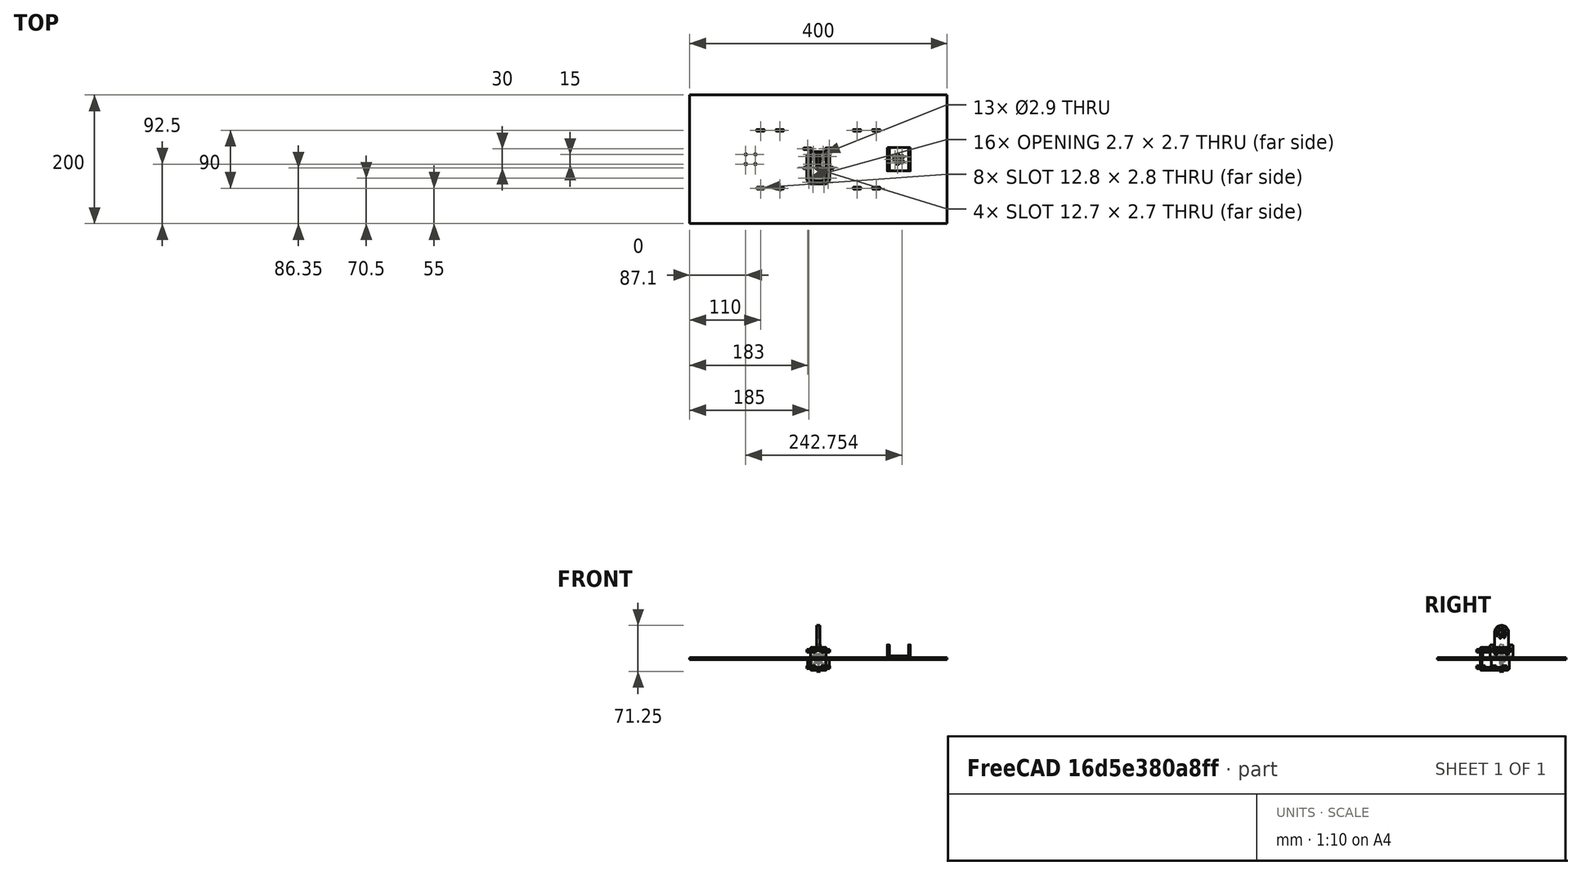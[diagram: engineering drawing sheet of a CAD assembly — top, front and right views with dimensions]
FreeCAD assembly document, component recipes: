
FREECAD ASSEMBLY — COMPONENT RECIPES ("Unnamed")

This assembly document has 8 components, labeled P0..P7 below (a component is one placed body or linked part). 6 of them carry a construction recipe — the FreeCAD feature program that regenerates the part from scratch, quoted from this document or its linked companion documents; the rest are supplied as boundary geometry only. No exploded tour is included for this assembly.
COMPONENT P0 — recipe-attached ("Body", modeled in this document).
Construction recipe (the document's own serialized feature program — sketch geometry with constraints, then the solid features built on it; lengths are millimeters unless a unit is written):

FEATURE [Sketcher::SketchObject] Sketch
  ArcFitTolerance = 1e-06
  AttachmentSupport = -> [Origin]
  ExternalTypes = [0]
  FullyConstrained = true
  MakeInternals = false
  MapMode = 5
  _ExternalGeoVersion = 1
  sketch-geometry (5):
    g0: LineSegment StartX=-200 StartY=-100 StartZ=0 EndX=200 EndY=-100 EndZ=0
    g1: LineSegment StartX=200 StartY=-100 StartZ=0 EndX=200 EndY=100 EndZ=0
    g2: LineSegment StartX=200 StartY=100 StartZ=0 EndX=-200 EndY=100 EndZ=0
    g3: LineSegment StartX=-200 StartY=100 StartZ=0 EndX=-200 EndY=-100 EndZ=0
    g4: GeomPoint [constr] X=0 Y=0 Z=0
  constraints (12):
    c: Coincident(g0,g1)
    c: Coincident(g1,g2)
    c: Coincident(g2,g3)
    c: Coincident(g3,g0)
    c: Horizontal(g0)
    c: Horizontal(g2)
    c: Vertical(g1)
    c: Vertical(g3)
    c: Symmetric(g2,g0,g4)
    c: Distance(g1,g3) = 400
    c: Distance(g0,g2) = 200
    c: Coincident(g4,g-1)
FEATURE [PartDesign::Pad] Pad
  Direction = (0,0,1)
  Length = 3
  Length2 = 10
  Profile = -> Sketch
  ReferenceAxis = -> Sketch [N_Axis]
  Refine = true
  SideType = 0
  Suppressed = false
  Type = 0
  Type2 = 0
FEATURE [Sketcher::SketchObject] Sketch001
  ArcFitTolerance = 1e-06
  AttachmentSupport = -> [Pad]
  ExternalTypes = [0]
  FullyConstrained = true
  MakeInternals = false
  MapMode = 5
  Placement = pos=(0,0,3) rot=(0,0,1;0rad)
  _ExternalGeoVersion = 1
  sketch-geometry (16):
    g0: ArcOfCircle CenterX=-12 CenterY=16.35 CenterZ=0 NormalX=0 NormalY=0 NormalZ=1 AngleXU=0 Radius=1.35 StartAngle=4.71239 EndAngle=7.85398
    g1: ArcOfCircle CenterX=-22 CenterY=16.35 CenterZ=0 NormalX=0 NormalY=0 NormalZ=1 AngleXU=0 Radius=1.35 StartAngle=1.5708 EndAngle=4.71239
    g2: LineSegment StartX=-12 StartY=15 StartZ=0 EndX=-22 EndY=15 EndZ=0
    g3: LineSegment StartX=-12 StartY=17.7 StartZ=0 EndX=-22 EndY=17.7 EndZ=0
    g4: ArcOfCircle CenterX=12 CenterY=16.35 CenterZ=0 NormalX=0 NormalY=0 NormalZ=1 AngleXU=0 Radius=1.35 StartAngle=1.5708 EndAngle=4.71239
    g5: ArcOfCircle CenterX=22 CenterY=16.35 CenterZ=0 NormalX=0 NormalY=0 NormalZ=1 AngleXU=0 Radius=1.35 StartAngle=4.71239 EndAngle=7.85398
    g6: LineSegment StartX=12 StartY=17.7 StartZ=0 EndX=22 EndY=17.7 EndZ=0
    g7: LineSegment StartX=12 StartY=15 StartZ=0 EndX=22 EndY=15 EndZ=0
    g8: ArcOfCircle CenterX=-22 CenterY=-13.65 CenterZ=0 NormalX=0 NormalY=0 NormalZ=1 AngleXU=0 Radius=1.35 StartAngle=1.5708 EndAngle=4.71239
    g9: ArcOfCircle CenterX=-12 CenterY=-13.65 CenterZ=0 NormalX=0 NormalY=0 NormalZ=1 AngleXU=0 Radius=1.35 StartAngle=4.71239 EndAngle=7.85398
    g10: LineSegment StartX=-22 StartY=-12.3 StartZ=0 EndX=-12 EndY=-12.3 EndZ=0
    g11: LineSegment StartX=-22 StartY=-15 StartZ=0 EndX=-12 EndY=-15 EndZ=0
    g12: ArcOfCircle CenterX=12 CenterY=-13.65 CenterZ=0 NormalX=0 NormalY=0 NormalZ=1 AngleXU=0 Radius=1.35 StartAngle=1.5708 EndAngle=4.71239
    g13: ArcOfCircle CenterX=22 CenterY=-13.65 CenterZ=0 NormalX=0 NormalY=0 NormalZ=1 AngleXU=0 Radius=1.35 StartAngle=4.71239 EndAngle=7.85398
    g14: LineSegment StartX=12 StartY=-12.3 StartZ=0 EndX=22 EndY=-12.3 EndZ=0
    g15: LineSegment StartX=12 StartY=-15 StartZ=0 EndX=22 EndY=-15 EndZ=0
  constraints (40):
    c: Tangent(g0,g2) = 1.5708
    c: Tangent(g0,g3) = -1.5708
    c: Tangent(g1,g2) = 1.5708
    c: Tangent(g1,g3) = -1.5708
    c: Equal(g0,g1)
    c: Distance(g0,g1) = 10
    c: Radius(g0) = 1.35
    c: Horizontal(g2)
    c: Distance(g0,g-2) = 12
    c: Tangent(g4,g6) = 1.5708
    c: Tangent(g4,g7) = -1.5708
    c: Tangent(g5,g6) = 1.5708
    c: Tangent(g5,g7) = -1.5708
    c: Equal(g4,g5)
    c: Distance(g4,g5) = 10
    c: Radius(g4) = 1.35
    c: Horizontal(g6)
    c: Distance(g4,g-2) = 12
    c: Distance(g-1,g7) = 15
    c: Distance(g-1,g2) = 15
    c: Tangent(g8,g10) = 1.5708
    c: Tangent(g8,g11) = -1.5708
    c: Tangent(g9,g10) = 1.5708
    c: Tangent(g9,g11) = -1.5708
    c: Equal(g8,g9)
    c: Distance(g8,g9) = 10
    c: Radius(g8) = 1.35
    c: Horizontal(g10)
    c: Distance(g9,g-2) = 12
    c: DistanceY(g9,g0) = 30
    c: Tangent(g12,g14) = 1.5708
    c: Tangent(g12,g15) = -1.5708
    c: Tangent(g13,g14) = 1.5708
    c: Tangent(g13,g15) = -1.5708
    c: Equal(g12,g13)
    c: Distance(g12,g13) = 10
    c: Radius(g12) = 1.35
    c: Horizontal(g14)
    c: Distance(g12,g-2) = 12
    c: Distance(g12,g4) = 30
FEATURE [PartDesign::Pocket] Pocket
  BaseFeature = -> Pad
  Direction = (0,0,-1)
  Length = 5
  Length2 = 5
  Profile = -> Sketch001
  ReferenceAxis = -> Sketch001 [N_Axis]
  Refine = true
  SideType = 0
  Suppressed = false
  Type = 0
  Type2 = 0
FEATURE [Sketcher::SketchObject] Sketch002
  ArcFitTolerance = 1e-06
  AttachmentSupport = -> [Pocket]
  ExternalTypes = [0]
  FullyConstrained = true
  MakeInternals = false
  MapMode = 5
  Placement = pos=(0,0,3) rot=(0,0,1;0rad)
  _ExternalGeoVersion = 1
  sketch-geometry (8):
    g0: ArcOfCircle CenterX=-55 CenterY=-45 CenterZ=0 NormalX=0 NormalY=0 NormalZ=1 AngleXU=0 Radius=1.4 StartAngle=4.71239 EndAngle=7.85398
    g1: ArcOfCircle CenterX=-65 CenterY=-45 CenterZ=0 NormalX=0 NormalY=0 NormalZ=1 AngleXU=0 Radius=1.4 StartAngle=1.5708 EndAngle=4.71239
    g2: LineSegment StartX=-55 StartY=-46.4 StartZ=0 EndX=-65 EndY=-46.4 EndZ=0
    g3: LineSegment StartX=-55 StartY=-43.6 StartZ=0 EndX=-65 EndY=-43.6 EndZ=0
    g4: ArcOfCircle CenterX=-85 CenterY=-45 CenterZ=0 NormalX=0 NormalY=0 NormalZ=1 AngleXU=0 Radius=1.4 StartAngle=4.71239 EndAngle=7.85398
    g5: ArcOfCircle CenterX=-95 CenterY=-45 CenterZ=0 NormalX=0 NormalY=0 NormalZ=1 AngleXU=0 Radius=1.4 StartAngle=1.5708 EndAngle=4.71239
    g6: LineSegment StartX=-85 StartY=-46.4 StartZ=0 EndX=-95 EndY=-46.4 EndZ=0
    g7: LineSegment StartX=-85 StartY=-43.6 StartZ=0 EndX=-95 EndY=-43.6 EndZ=0
  constraints (20):
    c: Tangent(g0,g2) = 1.5708
    c: Tangent(g0,g3) = -1.5708
    c: Tangent(g1,g2) = 1.5708
    c: Tangent(g1,g3) = -1.5708
    c: Equal(g0,g1)
    c: Distance(g0,g1) = 10
    c: Radius(g0) = 1.4
    c: Horizontal(g2)
    c: Distance(g0,g-2) = 55
    c: Distance(g0,g-1) = 45
    c: Tangent(g4,g6) = 1.5708
    c: Tangent(g4,g7) = -1.5708
    c: Tangent(g5,g6) = 1.5708
    c: Tangent(g5,g7) = -1.5708
    c: Equal(g4,g5)
    c: Distance(g4,g5) = 10
    c: Radius(g4) = 1.4
    c: Horizontal(g6)
    c: DistanceX(g4,g1) = 20
    c: Distance(g5,g-1) = 45
FEATURE [PartDesign::Pocket] Pocket001
  BaseFeature = -> Pocket
  Direction = (0,0,-1)
  Length = 5
  Length2 = 5
  Profile = -> Sketch002
  ReferenceAxis = -> Sketch002 [N_Axis]
  Refine = true
  SideType = 0
  Suppressed = false
  Type = 0
  Type2 = 0
FEATURE [PartDesign::Mirrored] Mirrored
  BaseFeature = -> Pocket001
  MirrorPlane = -> Sketch002 [V_Axis]
  Originals = -> [Pocket001]
  Refine = true
  Suppressed = false
  TransformMode = 0
FEATURE [PartDesign::Mirrored] Mirrored001
  BaseFeature = -> Mirrored
  MirrorPlane = -> Sketch002 [H_Axis]
  Originals = -> [Pocket001]
  Refine = true
  Suppressed = false
  TransformMode = 0
FEATURE [PartDesign::PolarPattern] PolarPattern
  Angle = 360
  Axis = -> Sketch002 [N_Axis]
  BaseFeature = -> Mirrored001
  Mode = 0
  Occurrences = 2
  Offset = 120
  Originals = -> [Pocket001]
  Refine = true
  SpacingPattern = [0]
  Spacings = [-1]
  Suppressed = false
  TransformMode = 0
FEATURE [Sketcher::SketchObject] Sketch006
  ArcFitTolerance = 1e-06
  AttachmentSupport = -> [PolarPattern]
  ExternalTypes = [0]
  FullyConstrained = true
  MakeInternals = false
  MapMode = 5
  Placement = pos=(0,0,3) rot=(0,0,1;0rad)
  _ExternalGeoVersion = 1
  sketch-geometry (5):
    g0: Circle CenterX=123.15 CenterY=5.7 CenterZ=0 NormalX=0 NormalY=0 NormalZ=1 AngleXU=0 Radius=1.25
    g1: Circle CenterX=119 CenterY=0 CenterZ=0 NormalX=0 NormalY=0 NormalZ=1 AngleXU=0 Radius=1.25
    g2: Circle CenterX=129.85 CenterY=3.55 CenterZ=0 NormalX=0 NormalY=0 NormalZ=1 AngleXU=0 Radius=1.25
    g3: Circle CenterX=123.15 CenterY=-5.7 CenterZ=0 NormalX=0 NormalY=0 NormalZ=1 AngleXU=0 Radius=1.25
    g4: Circle CenterX=129.85 CenterY=-3.52 CenterZ=0 NormalX=0 NormalY=0 NormalZ=1 AngleXU=0 Radius=1.25
  constraints (15):
    c: Diameter(g0) = 2.5
    c: PointOnObject(g1,g-1)
    c: Equal(g1,g0)
    c: Equal(g1,g3)
    c: Equal(g3,g4)
    c: Equal(g4,g2)
    c: DistanceX(g-1,g0) = 123.15
    c: DistanceX(g-1,g1) = 119
    c: DistanceX(g-1,g3) = 123.15
    c: DistanceX(g-1,g4) = 129.85
    c: DistanceX(g-1,g2) = 129.85
    c: Distance(g0,g-1) = 5.7
    c: Distance(g2,g-1) = 3.55
    c: Distance(g4,g-1) = 3.52
    c: Distance(g3,g-1) = 5.7
FEATURE [PartDesign::Hole] Hole001
  BaseFeature = -> PolarPattern
  BaseProfileType = 7
  CustomThreadClearance = 0
  Depth = 5
  DepthType = 0
  Diameter = 3.1
  DrillForDepth = false
  DrillPoint = 1
  DrillPointAngle = 118
  HoleCutCountersinkAngle = 90
  HoleCutCustomValues = false
  HoleCutDepth = 0
  HoleCutDiameter = 0
  HoleCutType = 0
  ModelThread = false
  Profile = -> Sketch006
  Refine = true
  Suppressed = false
  Tapered = false
  TaperedAngle = 90
  ThreadClass = 0
  ThreadDepth = 5
  ThreadDepthType = 0
  ThreadDiameter = 2.5
  ThreadDirection = 0
  ThreadFit = 2
  ThreadSize = 8
  ThreadType = 1
  Threaded = false
  UseCustomThreadClearance = false
FEATURE [Sketcher::SketchObject] Sketch011
  ArcFitTolerance = 1e-06
  AttachmentSupport = -> [Hole001]
  ExternalTypes = [0]
  FullyConstrained = true
  MakeInternals = false
  MapMode = 5
  Placement = pos=(0,0,3) rot=(0,0,1;0rad)
  _ExternalGeoVersion = 1
  sketch-geometry (5):
    g0: GeomPoint [constr] X=-105.4 Y=0 Z=0
    g1: Circle CenterX=-97.9 CenterY=7.49998 CenterZ=0 NormalX=0 NormalY=0 NormalZ=1 AngleXU=0 Radius=1.1
    g2: Circle CenterX=-112.9 CenterY=7.50002 CenterZ=0 NormalX=0 NormalY=0 NormalZ=1 AngleXU=0 Radius=1.1
    g3: Circle CenterX=-112.9 CenterY=-7.49998 CenterZ=0 NormalX=0 NormalY=0 NormalZ=1 AngleXU=0 Radius=1.1
    g4: Circle CenterX=-97.9 CenterY=-7.50002 CenterZ=0 NormalX=0 NormalY=0 NormalZ=1 AngleXU=0 Radius=1.1
  constraints (13):
    c: PointOnObject(g0,g-1)
    c: Symmetric(g1,g3,g0)
    c: Distance(g4,g3) = 15
    c: Distance(g3,g2) = 15
    c: Diameter(g1) = 2.2
    c: Equal(g1,g2)
    c: Equal(g2,g3)
    c: Equal(g3,g4)
    c: DistanceX(g1,g-1) = 97.9
    c: Distance(g1,g4) = 15
    c: DistanceX(g2,g1) = 15
    c: DistanceX(g3,g-1) = 112.9
    c: DistanceX(g4,g-1) = 97.9
FEATURE [PartDesign::Hole] Hole004
  BaseFeature = -> Hole001
  BaseProfileType = 7
  CustomThreadClearance = 0
  Depth = 5
  DepthType = 0
  Diameter = 2.9
  DrillForDepth = false
  DrillPoint = 1
  DrillPointAngle = 118
  HoleCutCountersinkAngle = 90
  HoleCutCustomValues = false
  HoleCutDepth = 0
  HoleCutDiameter = 0
  HoleCutType = 0
  ModelThread = false
  Profile = -> Sketch011
  Refine = true
  Suppressed = false
  Tapered = false
  TaperedAngle = 90
  ThreadClass = 0
  ThreadDepth = 5
  ThreadDepthType = 0
  ThreadDiameter = 2.5
  ThreadDirection = 0
  ThreadFit = 0
  ThreadSize = 8
  ThreadType = 1
  Threaded = false
  UseCustomThreadClearance = false
FEATURE [PartDesign::Body] Body  label="base"
  AllowCompound = true
  Group = -> [Sketch,Pad,Sketch001,Pocket,Sketch002,Pocket001,Mirrored,Mirrored001,PolarPattern,Sketch006,Hole001,Sketch011,Hole004]
  Origin = -> Origin
  Tip = -> Hole004
COMPONENT P1 — geometry summary ("HN07_I_002"; no construction recipe available for this part):
  bounding box: 22.0 x 22.0 x 3.1 mm
  tessellated surface: 6,696 triangles
  volume: 557 mm^3 (38% of its bounding box)
  symmetry: 4-fold rotationally symmetric about the x axis
COMPONENT P2 — same part as P0; its construction recipe is shown at P0.
COMPONENT P3 — recipe-attached ("horn_holder001", modeled in this document).
Construction recipe (the document's own serialized feature program — sketch geometry with constraints, then the solid features built on it; lengths are millimeters unless a unit is written):

FEATURE [Sketcher::SketchObject] Sketch012
  ArcFitTolerance = 1e-06
  AttachmentSupport = -> [Origin013]
  ExternalTypes = [0]
  FullyConstrained = true
  MakeInternals = false
  MapMode = 5
  _ExternalGeoVersion = 1
  sketch-geometry (5):
    g0: LineSegment StartX=-12 StartY=-12 StartZ=0 EndX=12 EndY=-12 EndZ=0
    g1: LineSegment StartX=12 StartY=-12 StartZ=0 EndX=12 EndY=12 EndZ=0
    g2: LineSegment StartX=12 StartY=12 StartZ=0 EndX=-12 EndY=12 EndZ=0
    g3: LineSegment StartX=-12 StartY=12 StartZ=0 EndX=-12 EndY=-12 EndZ=0
    g4: GeomPoint [constr] X=0 Y=0 Z=0
  constraints (12):
    c: Coincident(g0,g1)
    c: Coincident(g1,g2)
    c: Coincident(g2,g3)
    c: Coincident(g3,g0)
    c: Horizontal(g0)
    c: Horizontal(g2)
    c: Vertical(g1)
    c: Vertical(g3)
    c: Symmetric(g2,g0,g4)
    c: Distance(g1,g3) = 24
    c: Distance(g0,g2) = 24
    c: Coincident(g4,g-1)
FEATURE [PartDesign::Pad] Pad003
  Direction = (0,0,1)
  Length = 5
  Length2 = 10
  Profile = -> Sketch012
  ReferenceAxis = -> Sketch012 [N_Axis]
  Refine = true
  SideType = 0
  Suppressed = false
  Type = 0
  Type2 = 0
FEATURE [Sketcher::SketchObject] Sketch013
  ArcFitTolerance = 1e-06
  AttachmentSupport = -> [Pad003]
  ExternalTypes = [0]
  FullyConstrained = true
  MakeInternals = false
  MapMode = 5
  Placement = pos=(0,0,5) rot=(0,0,1;0rad)
  _ExternalGeoVersion = 1
  sketch-geometry (5):
    g0: GeomPoint [constr] X=0 Y=0 Z=0
    g1: Circle CenterX=7.5 CenterY=7.5 CenterZ=0 NormalX=0 NormalY=0 NormalZ=1 AngleXU=0 Radius=1.1
    g2: Circle CenterX=-7.5 CenterY=7.5 CenterZ=0 NormalX=0 NormalY=0 NormalZ=1 AngleXU=0 Radius=1.1
    g3: Circle CenterX=-7.5 CenterY=-7.5 CenterZ=0 NormalX=0 NormalY=0 NormalZ=1 AngleXU=0 Radius=1.1
    g4: Circle CenterX=7.5 CenterY=-7.5 CenterZ=0 NormalX=0 NormalY=0 NormalZ=1 AngleXU=0 Radius=1.1
  constraints (12):
    c: Symmetric(g1,g3,g0)
    c: Distance(g4,g3) = 15
    c: Distance(g3,g2) = 15
    c: Coincident(g0,g-1)
    c: Diameter(g1) = 2.2
    c: Equal(g1,g2)
    c: Equal(g2,g3)
    c: Equal(g3,g4)
    c: DistanceX(g2,g1) = 15
    c: DistanceY(g4,g1) = 15
    c: Distance(g4,g-2) = 7.5
    c: Distance(g2,g-1) = 7.5
FEATURE [PartDesign::Hole] Hole005
  BaseFeature = -> Pad003
  BaseProfileType = 7
  CustomThreadClearance = 0
  Depth = 5
  DepthType = 0
  Diameter = 2.9
  DrillForDepth = false
  DrillPoint = 1
  DrillPointAngle = 118
  HoleCutCountersinkAngle = 90
  HoleCutCustomValues = false
  HoleCutDepth = 0
  HoleCutDiameter = 0
  HoleCutType = 0
  ModelThread = false
  Profile = -> Sketch013
  Refine = true
  Suppressed = false
  Tapered = false
  TaperedAngle = 90
  ThreadClass = 0
  ThreadDepth = 5
  ThreadDepthType = 0
  ThreadDiameter = 2.5
  ThreadDirection = 0
  ThreadFit = 0
  ThreadSize = 8
  ThreadType = 1
  Threaded = false
  UseCustomThreadClearance = false
FEATURE [Sketcher::SketchObject] Sketch014
  ArcFitTolerance = 1e-06
  AttachmentSupport = -> [Hole005]
  ExternalTypes = [0]
  FullyConstrained = true
  MakeInternals = false
  MapMode = 5
  Placement = pos=(0,0,5) rot=(0,0,1;0rad)
  _ExternalGeoVersion = 1
  sketch-geometry (5):
    g0: LineSegment StartX=-2.5 StartY=-11 StartZ=0 EndX=2.5 EndY=-11 EndZ=0
    g1: LineSegment StartX=2.5 StartY=-11 StartZ=0 EndX=2.5 EndY=11 EndZ=0
    g2: LineSegment StartX=2.5 StartY=11 StartZ=0 EndX=-2.5 EndY=11 EndZ=0
    g3: LineSegment StartX=-2.5 StartY=11 StartZ=0 EndX=-2.5 EndY=-11 EndZ=0
    g4: GeomPoint [constr] X=0 Y=0 Z=0
  constraints (12):
    c: Coincident(g0,g1)
    c: Coincident(g1,g2)
    c: Coincident(g2,g3)
    c: Coincident(g3,g0)
    c: Horizontal(g0)
    c: Horizontal(g2)
    c: Vertical(g1)
    c: Vertical(g3)
    c: Symmetric(g2,g0,g4)
    c: Distance(g1,g3) = 5
    c: Distance(g0,g2) = 22
    c: Coincident(g4,g-1)
FEATURE [PartDesign::Pad] Pad004
  BaseFeature = -> Hole005
  Direction = (0,0,1)
  Length = 37
  Length2 = 10
  Profile = -> Sketch014
  ReferenceAxis = -> Sketch014 [N_Axis]
  Refine = true
  SideType = 0
  Suppressed = false
  Type = 0
  Type2 = 0
FEATURE [PartDesign::Fillet] Fillet
  Base = -> Pad004 [Edge23,Edge21]
  BaseFeature = -> Pad004
  Radius = 3
  Refine = true
  SupportTransform = false
  Suppressed = false
  UseAllEdges = false
FEATURE [Sketcher::SketchObject] Sketch015
  ArcFitTolerance = 1e-06
  AttachmentSupport = -> [Fillet]
  ExternalTypes = [0,0]
  FullyConstrained = true
  MakeInternals = false
  MapMode = 5
  Placement = pos=(-2.5,0,0) rot=(0.57735,-0.57735,-0.57735;2.0944rad)
  _ExternalGeoVersion = 1
  sketch-geometry (2):
    g0: ArcOfCircle CenterX=6.6e-13 CenterY=42 CenterZ=0 NormalX=0 NormalY=0 NormalZ=1 AngleXU=0 Radius=11 StartAngle=0 EndAngle=3.14159
    g1: LineSegment StartX=-11 StartY=42 StartZ=0 EndX=11 EndY=42 EndZ=0
  constraints (7):
    c: Coincident(g1,g0)
    c: Coincident(g1,g0)
    c: DistanceY(g-1,g0) = 42
    c: DistanceY(g-1,g0) = 42
    c: Distance(g0,g-2) = 11
    c: Distance(g0,g-2) = 11
    c: Distance(g0,g-1) = 31
FEATURE [PartDesign::Pad] Pad005
  BaseFeature = -> Fillet
  Direction = (-1,0,0)
  Length = 5
  Length2 = 10
  Profile = -> Sketch015
  ReferenceAxis = -> Sketch015 [N_Axis]
  Refine = true
  Reversed = true
  SideType = 0
  Suppressed = false
  Type = 0
  Type2 = 0
FEATURE [Sketcher::SketchObject] Sketch016
  ArcFitTolerance = 1e-06
  AttachmentSupport = -> [Pad005]
  ExternalTypes = [0]
  FullyConstrained = true
  MakeInternals = false
  MapMode = 5
  Placement = pos=(2.5,0,0) rot=(0.57735,0.57735,0.57735;2.0944rad)
  _ExternalGeoVersion = 1
  sketch-geometry (8):
    g0: Circle CenterX=-6.87 CenterY=37.91 CenterZ=0 NormalX=0 NormalY=0 NormalZ=1 AngleXU=0 Radius=0.75
    g1: Circle CenterX=-7.75 CenterY=43.96 CenterZ=0 NormalX=0 NormalY=0 NormalZ=1 AngleXU=0 Radius=0.75
    g2: Circle CenterX=-4.1 CenterY=48.87 CenterZ=0 NormalX=0 NormalY=0 NormalZ=1 AngleXU=0 Radius=0.75
    g3: Circle CenterX=1.96 CenterY=49.75 CenterZ=0 NormalX=0 NormalY=0 NormalZ=1 AngleXU=0 Radius=0.75
    g4: Circle CenterX=6.87 CenterY=46.09 CenterZ=0 NormalX=0 NormalY=0 NormalZ=1 AngleXU=0 Radius=0.75
    g5: Circle CenterX=7.75 CenterY=40.04 CenterZ=0 NormalX=0 NormalY=0 NormalZ=1 AngleXU=0 Radius=0.75
    g6: Circle CenterX=4.1 CenterY=35.13 CenterZ=0 NormalX=0 NormalY=0 NormalZ=1 AngleXU=0 Radius=0.75
    g7: Circle CenterX=-1.97 CenterY=34.24 CenterZ=0 NormalX=0 NormalY=0 NormalZ=1 AngleXU=0 Radius=0.75
  constraints (24):
    c: Diameter(g0) = 1.5
    c: Distance(g0,g-2) = 6.87
    c: Distance(g0,g-1) = 37.91
    c: Equal(g0,g1)
    c: Equal(g1,g2)
    c: Equal(g2,g3)
    c: Equal(g3,g4)
    c: Equal(g4,g5)
    c: Equal(g5,g6)
    c: Equal(g6,g7)
    c: Distance(g1,g-2) = 7.75
    c: Distance(g2,g-2) = 4.1
    c: Distance(g3,g-2) = 1.96
    c: Distance(g4,g-2) = 6.87
    c: Distance(g5,g-2) = 7.75
    c: Distance(g6,g-2) = 4.1
    c: Distance(g7,g-2) = 1.97
    c: Distance(g7,g-1) = 34.24
    c: DistanceY(g-1,g1) = 43.96
    c: DistanceY(g-1,g2) = 48.87
    c: DistanceY(g-1,g3) = 49.75
    c: DistanceY(g-1,g4) = 46.09
    c: DistanceY(g-1,g5) = 40.04
    c: DistanceY(g-1,g6) = 35.13
FEATURE [PartDesign::Hole] Hole006
  BaseFeature = -> Pad005
  BaseProfileType = 7
  CustomThreadClearance = 0
  Depth = 5
  DepthType = 0
  Diameter = 2.552
  DrillForDepth = false
  DrillPoint = 1
  DrillPointAngle = 118
  HoleCutCountersinkAngle = 90
  HoleCutCustomValues = false
  HoleCutDepth = 0
  HoleCutDiameter = 0
  HoleCutType = 0
  ModelThread = false
  Profile = -> Sketch016
  Refine = true
  Suppressed = false
  Tapered = false
  TaperedAngle = 90
  ThreadClass = 0
  ThreadDepth = 5
  ThreadDepthType = 0
  ThreadDiameter = 2.2
  ThreadDirection = 0
  ThreadFit = 2
  ThreadSize = 7
  ThreadType = 1
  Threaded = false
  UseCustomThreadClearance = false
FEATURE [Sketcher::SketchObject] Sketch017
  ArcFitTolerance = 1e-06
  AttachmentSupport = -> [Hole006]
  ExternalTypes = [0,0]
  FullyConstrained = true
  MakeInternals = false
  MapMode = 5
  Placement = pos=(2.5,0,0) rot=(0.57735,0.57735,0.57735;2.0944rad)
  _ExternalGeoVersion = 1
  sketch-geometry (1):
    g0: Circle CenterX=0 CenterY=42 CenterZ=0 NormalX=0 NormalY=0 NormalZ=1 AngleXU=0 Radius=5.5
  constraints (3):
    c: Diameter(g0) = 11
    c: PointOnObject(g0,g-2)
    c: DistanceY(g-1,g0) = 42
FEATURE [PartDesign::Hole] Hole002
  BaseFeature = -> Hole006
  BaseProfileType = 7
  CustomThreadClearance = 0
  Depth = 2.5
  DepthType = 0
  Diameter = 9
  DrillForDepth = false
  DrillPoint = 1
  DrillPointAngle = 118
  HoleCutCountersinkAngle = 90
  HoleCutCustomValues = false
  HoleCutDepth = 0
  HoleCutDiameter = 0
  HoleCutType = 0
  ModelThread = false
  Profile = -> Sketch017
  Refine = true
  Suppressed = false
  Tapered = false
  TaperedAngle = 90
  ThreadClass = 0
  ThreadDepth = 2.5
  ThreadDepthType = 0
  ThreadDiameter = 8
  ThreadDirection = 0
  ThreadFit = 0
  ThreadSize = 16
  ThreadType = 1
  Threaded = false
  UseCustomThreadClearance = false
FEATURE [Sketcher::SketchObject] Sketch018
  ArcFitTolerance = 1e-06
  AttachmentSupport = -> [Hole002]
  ExternalTypes = [0]
  FullyConstrained = true
  MakeInternals = false
  MapMode = 5
  Placement = pos=(-2.5,0,0) rot=(0.57735,-0.57735,-0.57735;2.0944rad)
  _ExternalGeoVersion = 1
  sketch-geometry (1):
    g0: Circle CenterX=0 CenterY=41.6 CenterZ=0 NormalX=0 NormalY=0 NormalZ=1 AngleXU=0 Radius=1.1
  constraints (3):
    c: Diameter(g0) = 2.2
    c: PointOnObject(g0,g-2)
    c: DistanceY(g-1,g0) = 41.6
FEATURE [PartDesign::Hole] Hole007
  BaseFeature = -> Hole002
  BaseProfileType = 7
  CustomThreadClearance = 0
  Depth = 2.5
  DepthType = 0
  Diameter = 2.9
  DrillForDepth = false
  DrillPoint = 1
  DrillPointAngle = 118
  HoleCutCountersinkAngle = 90
  HoleCutCustomValues = false
  HoleCutDepth = 0
  HoleCutDiameter = 0
  HoleCutType = 0
  ModelThread = false
  Profile = -> Sketch018
  Refine = true
  Suppressed = false
  Tapered = false
  TaperedAngle = 90
  ThreadClass = 0
  ThreadDepth = 2.5
  ThreadDepthType = 0
  ThreadDiameter = 2.5
  ThreadDirection = 0
  ThreadFit = 0
  ThreadSize = 8
  ThreadType = 1
  Threaded = false
  UseCustomThreadClearance = false
FEATURE [PartDesign::Body] Body002  label="horn_holder"
  AllowCompound = true
  Group = -> [Sketch012,Pad003,Sketch013,Hole005,Sketch014,Pad004,Fillet,Sketch015,Pad005,Sketch016,Hole006,Sketch017,Hole002,Sketch018,Hole007]
  Origin = -> Origin013
  Tip = -> Hole007
COMPONENT P4 — same part as P3; its construction recipe is shown at P3.
COMPONENT P5 — same part as P3; its construction recipe is shown at P3.
COMPONENT P6 — geometry summary ("mx001"; no construction recipe available for this part):
  bounding box: 50.6 x 43.3 x 35.6 mm
  tessellated surface: 32,846 triangles
  volume: 44571 mm^3 (57% of its bounding box)
COMPONENT P7 — recipe-attached ("mx_28_holder001", modeled in this document).
Construction recipe (the document's own serialized feature program — sketch geometry with constraints, then the solid features built on it; lengths are millimeters unless a unit is written):

FEATURE [PartDesign::ShapeBinder] CopyPart__Feature
  TraceSupport = false
FEATURE [Sketcher::SketchObject] Sketch003
  ArcFitTolerance = 1e-06
  AttachmentSupport = -> [CopyPart__Feature]
  ExternalTypes = [0]
  FullyConstrained = true
  MakeInternals = false
  MapMode = 5
  Placement = pos=(0,-38.6,0) rot=(1,0,0;1.5708rad)
  _ExternalGeoVersion = 1
  sketch-geometry (5):
    g0: LineSegment StartX=-18 StartY=-15 StartZ=0 EndX=18 EndY=-15 EndZ=0
    g1: LineSegment StartX=18 StartY=-15 StartZ=0 EndX=18 EndY=15 EndZ=0
    g2: LineSegment StartX=18 StartY=15 StartZ=0 EndX=-18 EndY=15 EndZ=0
    g3: LineSegment StartX=-18 StartY=15 StartZ=0 EndX=-18 EndY=-15 EndZ=0
    g4: GeomPoint [constr] X=0 Y=0 Z=0
  constraints (12):
    c: Coincident(g0,g1)
    c: Coincident(g1,g2)
    c: Coincident(g2,g3)
    c: Coincident(g3,g0)
    c: Horizontal(g0)
    c: Horizontal(g2)
    c: Vertical(g1)
    c: Vertical(g3)
    c: Symmetric(g2,g0,g4)
    c: Distance(g1,g3) = 36
    c: Distance(g0,g2) = 30
    c: Coincident(g4,g-1)
FEATURE [PartDesign::Pad] Pad001
  Direction = (0,-1,2e-16)
  Length = 3
  Length2 = 10
  Profile = -> Sketch003
  ReferenceAxis = -> Sketch003 [N_Axis]
  Refine = true
  SideType = 0
  Suppressed = false
  Type = 0
  Type2 = 0
FEATURE [Sketcher::SketchObject] Sketch004
  ArcFitTolerance = 1e-06
  AttachmentSupport = -> [Pad001]
  ExternalTypes = [0]
  FullyConstrained = true
  MakeInternals = false
  MapMode = 5
  Placement = pos=(0,3.3e-15,15) rot=(0,0,1;0rad)
  _ExternalGeoVersion = 1
  sketch-geometry (12):
    g0: LineSegment StartX=-18 StartY=-21.6 StartZ=0 EndX=-12.5 EndY=-21.6 EndZ=0
    g1: LineSegment StartX=-12.5 StartY=-21.6 StartZ=0 EndX=-12.5 EndY=-33.6 EndZ=0
    g2: LineSegment StartX=-12.5 StartY=-33.6 StartZ=0 EndX=12.5 EndY=-33.6 EndZ=0
    g3: LineSegment StartX=12.5 StartY=-33.6 StartZ=0 EndX=12.5 EndY=-21.6 EndZ=0
    g4: LineSegment StartX=12.5 StartY=-21.6 StartZ=0 EndX=18 EndY=-21.6 EndZ=0
    g5: LineSegment StartX=18 StartY=-21.6 StartZ=0 EndX=18 EndY=-41.6 EndZ=0
    g6: LineSegment StartX=18 StartY=-41.6 StartZ=0 EndX=-18 EndY=-41.6 EndZ=0
    g7: LineSegment StartX=-18 StartY=-41.6 StartZ=0 EndX=-18 EndY=-21.6 EndZ=0
    g8: Circle CenterX=-15 CenterY=-29.5 CenterZ=0 NormalX=0 NormalY=0 NormalZ=1 AngleXU=0 Radius=1.5
    g9: Circle CenterX=-8.5 CenterY=-35.8 CenterZ=0 NormalX=0 NormalY=0 NormalZ=1 AngleXU=0 Radius=1.5
    g10: Circle CenterX=8.5 CenterY=-35.8 CenterZ=0 NormalX=0 NormalY=0 NormalZ=1 AngleXU=0 Radius=1.5
    g11: Circle CenterX=15 CenterY=-29.5 CenterZ=0 NormalX=0 NormalY=0 NormalZ=1 AngleXU=0 Radius=1.5
  constraints (36):
    c: Horizontal(g0)
    c: Coincident(g0,g1)
    c: Vertical(g1)
    c: Coincident(g1,g2)
    c: Horizontal(g2)
    c: Coincident(g2,g3)
    c: Vertical(g3)
    c: Coincident(g3,g4)
    c: Horizontal(g4)
    c: Coincident(g4,g5)
    c: Vertical(g5)
    c: Coincident(g5,g6)
    c: Horizontal(g6)
    c: Coincident(g6,g7)
    c: Coincident(g7,g0)
    c: Vertical(g7)
    c: DistanceX(g6,g6) = 36
    c: DistanceY(g7,g7) = 20
    c: Distance(g3,g1) = 25
    c: Equal(g0,g4)
    c: Equal(g3,g1)
    c: Distance(g-1,g6) = 41.6
    c: Distance(g-2,g7) = 18
    c: Distance(g6,g2) = 8
    c: Diameter(g8) = 3
    c: Equal(g8,g9)
    c: Equal(g9,g10)
    c: Equal(g10,g11)
    c: Distance(g8,g7) = 3
    c: Distance(g9,g6) = 5.8
    c: Distance(g9,g7) = 9.5
    c: Distance(g10,g5) = 9.5
    c: Distance(g10,g6) = 5.8
    c: Distance(g11,g5) = 3
    c: Distance(g8,g0) = 7.9
    c: Distance(g11,g4) = 7.9
FEATURE [PartDesign::Pad] Pad002
  BaseFeature = -> Pad001
  Direction = (0,0,1)
  Length = 3
  Length2 = 10
  Profile = -> Sketch004
  ReferenceAxis = -> Sketch004 [N_Axis]
  Refine = true
  SideType = 0
  Suppressed = false
  Type = 0
  Type2 = 0
FEATURE [PartDesign::Mirrored] Mirrored002
  BaseFeature = -> Pad002
  MirrorPlane = -> XY_Plane001
  Originals = -> [Pad002]
  Refine = true
  Suppressed = false
  TransformMode = 0
FEATURE [PartDesign::Fillet] Fillet001
  Base = -> Mirrored002 [Edge60,Edge47,Edge36,Edge27]
  BaseFeature = -> Mirrored002
  Radius = 2
  Refine = true
  SupportTransform = false
  Suppressed = false
  UseAllEdges = false
FEATURE [PartDesign::Fillet] Fillet002
  Base = -> Fillet001 [Edge51,Edge56]
  BaseFeature = -> Fillet001
  Radius = 1
  Refine = true
  SupportTransform = false
  Suppressed = false
  UseAllEdges = false
FEATURE [Sketcher::SketchObject] Sketch005
  ArcFitTolerance = 1e-06
  AttachmentSupport = -> [Fillet002]
  ExternalTypes = [0]
  FullyConstrained = true
  MakeInternals = false
  MapMode = 5
  Placement = pos=(0,-38.6,0) rot=(0,0.707107,0.707107;3.14159rad)
  _ExternalGeoVersion = 1
  sketch-geometry (1):
    g0: Circle CenterX=0 CenterY=6 CenterZ=0 NormalX=0 NormalY=0 NormalZ=1 AngleXU=0 Radius=1.25
  constraints (3):
    c: Diameter(g0) = 2.5
    c: PointOnObject(g0,g-2)
    c: Distance(g0,g-1) = 6
FEATURE [PartDesign::Hole] Hole
  BaseFeature = -> Fillet002
  BaseProfileType = 7
  CustomThreadClearance = 0
  Depth = 5
  DepthType = 0
  Diameter = 2.9
  DrillForDepth = false
  DrillPoint = 1
  DrillPointAngle = 118
  HoleCutCountersinkAngle = 90
  HoleCutCustomValues = false
  HoleCutDepth = 2.65
  HoleCutDiameter = 5.3
  HoleCutType = 7
  ModelThread = false
  Profile = -> Sketch005
  Refine = true
  Suppressed = false
  Tapered = false
  TaperedAngle = 90
  ThreadClass = 0
  ThreadDepth = 5
  ThreadDepthType = 0
  ThreadDiameter = 2.5
  ThreadDirection = 0
  ThreadFit = 0
  ThreadSize = 8
  ThreadType = 1
  Threaded = false
  UseCustomThreadClearance = false
FEATURE [PartDesign::PolarPattern] PolarPattern001
  Angle = 360
  Axis = -> Sketch005 [N_Axis]
  BaseFeature = -> Hole
  Mode = 0
  Occurrences = 5
  Offset = 120
  Originals = -> [Hole]
  Refine = true
  SpacingPattern = [0]
  Spacings = [-1,-1,-1,-1]
  Suppressed = false
  TransformMode = 0
FEATURE [PartDesign::Body] Body001  label="mx_28_holder"
  AllowCompound = true
  Group = -> [CopyPart__Feature,Sketch003,Pad001,Sketch004,Pad002,Mirrored002,Fillet001,Fillet002,Sketch005,Hole,PolarPattern001]
  Origin = -> Origin002
  Placement = pos=(125,5.4e-15,44.5) rot=(-0.57735,0.57735,0.57735;4.18879rad)
  Tip = -> PolarPattern001
PROVENANCE & LICENSES
A FreeCAD (.FCStd) document from a public repository crawl; recipes are the document's own serialized feature recipes (and, for linked parts, companion documents' recipes).
License: mit.
